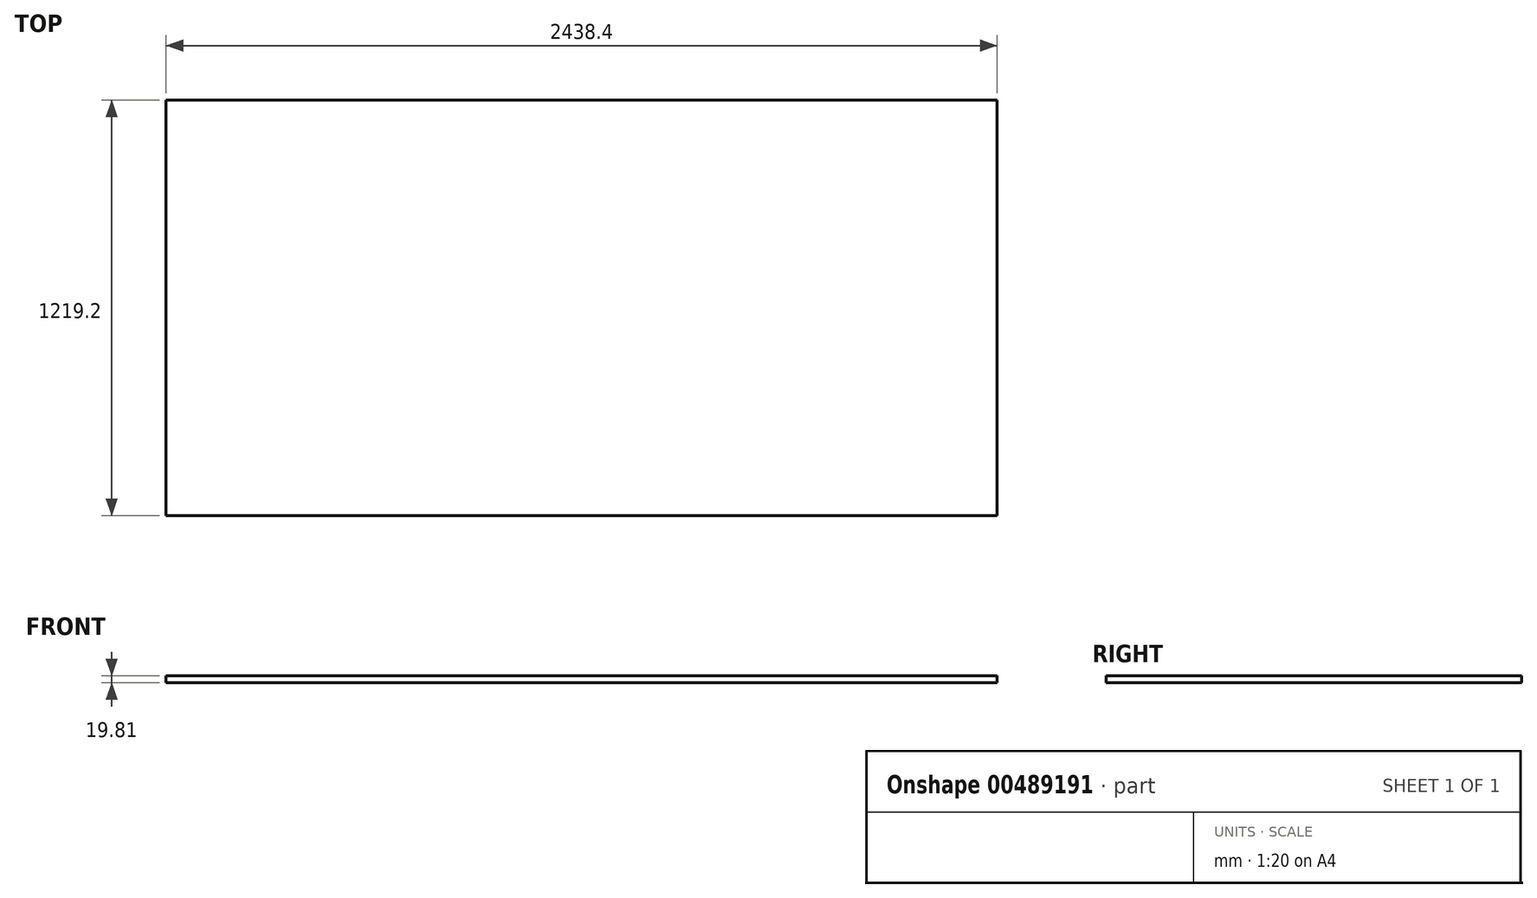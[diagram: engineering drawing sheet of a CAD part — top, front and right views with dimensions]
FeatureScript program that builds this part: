
annotation { "Feature Type Name" : "Feature", "Feature Type Description" : "" }
export const myFeature = defineFeature(function(context is Context, id is Id, definition is map)
    precondition{}
    {
        {
            var Q0;
            Q0=qCreatedBy(makeId("Top.planeOp"),FACE);
            var sketch = newSketch(context, id + "F0", { "sketchPlane" : qUnion([Q0])});
            skLineSegment(sketch, "E0.bottom", {"start": v(-1217.14, -982.83) * mm, "end": v(1221.26, -982.83) * mm});
            skLineSegment(sketch, "E0.top", {"start": v(-1217.14, 236.37) * mm, "end": v(1221.26, 236.37) * mm});
            skLineSegment(sketch, "E0.left", {"start": v(-1217.14, -982.83) * mm, "end": v(-1217.14, 236.37) * mm});
            skLineSegment(sketch, "E0.right", {"start": v(1221.26, -982.83) * mm, "end": v(1221.26, 236.37) * mm});
            skSolve(sketch);
        }
        {
            var Q0;
            Q0=makeQuery(id+"F0.imprint","IMPRINT",FACE,{"disambiguationData":[TD([[makeQuery(id+"F0.imprint","IMPRINT",EDGE,{"derivedFrom":sQuery(id+"F0.wireOp",EDGE,"E0.bottom")}),1.0]])]});
            extrude(context, id + "F1", {"entities" : qUnion([Q0]), "depth" : 19.8 * mm, "offsetDistance" : 25.4 * mm});
        }
    });
